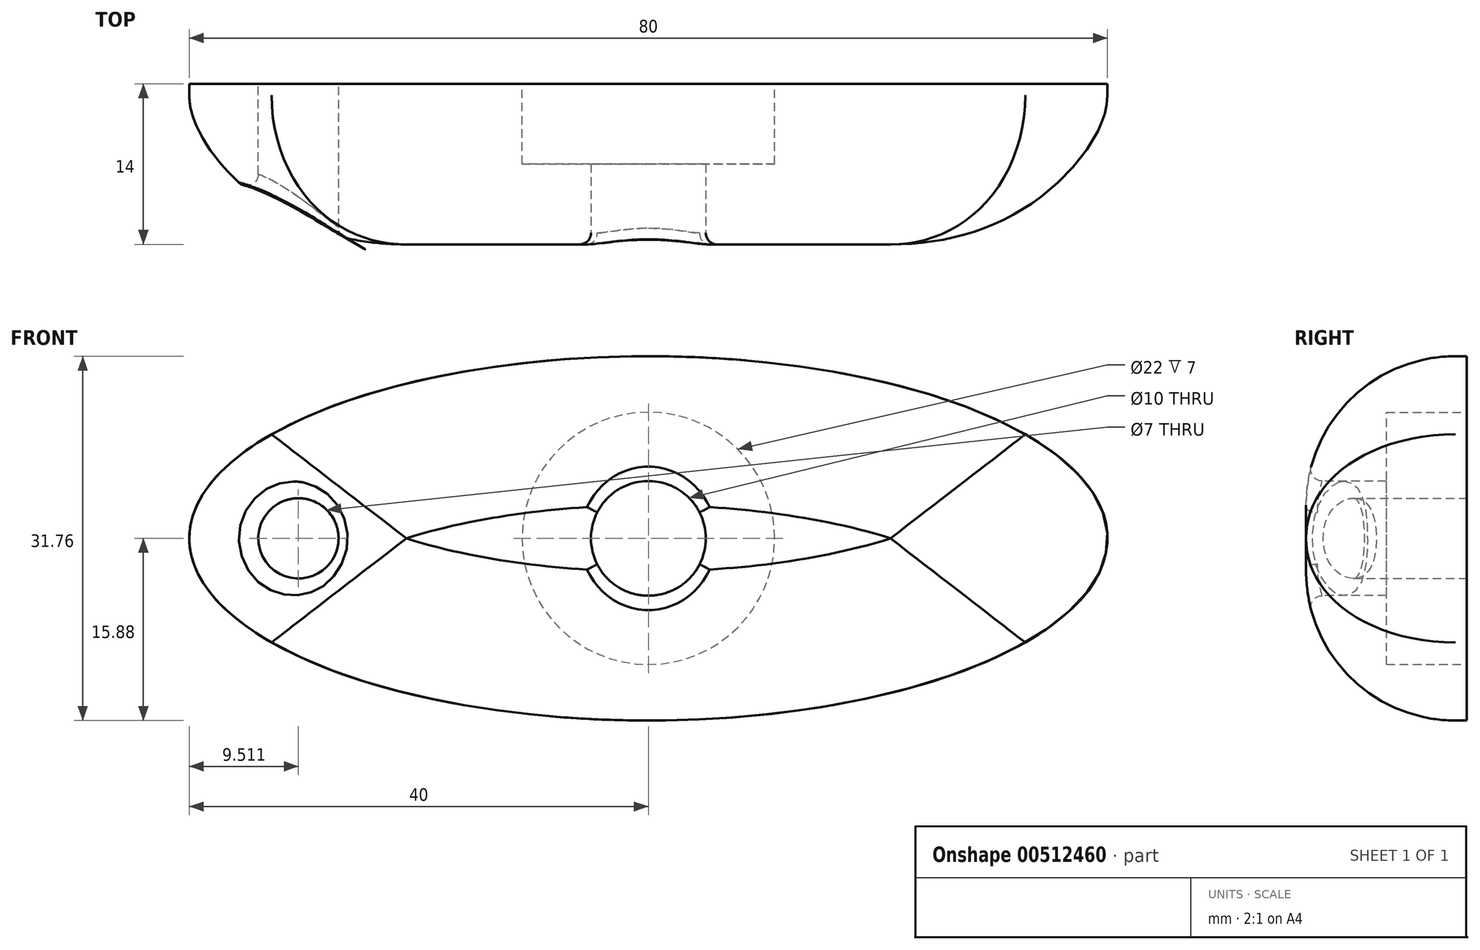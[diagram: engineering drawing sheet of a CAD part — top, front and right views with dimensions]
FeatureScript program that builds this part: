
annotation { "Feature Type Name" : "Feature", "Feature Type Description" : "" }
export const myFeature = defineFeature(function(context is Context, id is Id, definition is map)
    precondition{}
    {
        {
            var Q0;
            Q0=qCreatedBy(makeId("Front.planeOp"),FACE);
            var sketch = newSketch(context, id + "F0", { "sketchPlane" : qUnion([Q0])});
            skEllipse(sketch, "E0", {"center": v(0, 0) * mm, "majorRadius": 40 * mm, "minorRadius": 15.88 * mm, "majorAxis": v(-1, 0)});
            skCircle(sketch, "E1", {"center": v(0, 0) * mm, "radius": 11 * mm});
            skSolve(sketch);
        }
        {
            var Q0;
            Q0 = qSketchRegion(id + "F0", true);
            extrude(context, id + "F1", {"entities" : qUnion([Q0]), "depth" : 14 * mm});
        }
        {
            var Q0;
            Q0=makeQuery(id+"F1.opExtrude","CAP_FACE",FACE,{"disambiguationData":[OSD([sQuery(id+"F0.wireOp",EDGE,"E0"),sQuery(id+"F0.wireOp",EDGE,"E1")])],"isStart":false});
            var sketch = newSketch(context, id + "F2", { "sketchPlane" : qUnion([Q0])});
            skCircle(sketch, "E2", {"center": v(0, 0) * mm, "radius": 5 * mm});
            skSolve(sketch);
        }
        {
            var Q0;
            Q0=makeQuery(id+"F2.imprint","IMPRINT",FACE,{"disambiguationData":[TD([[makeQuery(id+"F2.imprint","IMPRINT",EDGE,{"derivedFrom":sQuery(id+"F2.wireOp",EDGE,"E2")}),-1.0]])]});
            extrude(context, id + "F3", {"entities" : qUnion([Q0]), "operationType" : NewBodyOperationType.ADD, "oppositeDirection" : true, "depth" : 7 * mm});
        }
        {
            var Q0;
            Q0=makeQuery(id+"F1.opExtrude","CAP_EDGE",EDGE,{"disambiguationData":[OSD([sQuery(id+"F0.wireOp",EDGE,"E0")])],"isStart":false});
            fillet(context, id + "F4", {"entities" : qUnion([Q0]), "radius" : 13 * mm, "tangentPropagation" : true, "allowEdgeOverflow" : false});
        }
        {
            var Q0;
            Q0=makeQuery(id+"F1.opExtrude","CAP_FACE",FACE,{"disambiguationData":[OSD([sQuery(id+"F0.wireOp",EDGE,"E0"),sQuery(id+"F0.wireOp",EDGE,"E1")])],"isStart":true});
            var sketch = newSketch(context, id + "F5", { "sketchPlane" : qUnion([Q0])});
            skCircle(sketch, "E3", {"center": v(30.49, 0) * mm, "radius": 3.5 * mm});
            skSolve(sketch);
        }
        {
            var Q0;
            Q0=makeQuery(id+"F5.imprint","IMPRINT",FACE,{"disambiguationData":[TD([[makeQuery(id+"F5.imprint","IMPRINT",EDGE,{"derivedFrom":sQuery(id+"F5.wireOp",EDGE,"E3")}),1.0]])]});
            extrude(context, id + "F6", {"entities" : qUnion([Q0]), "operationType" : NewBodyOperationType.REMOVE, "endBound" : BoundingType.THROUGH_ALL, "oppositeDirection" : true, "depth" : 25 * mm});
        }
        {
            var Q0;
            Q0=makeQuery(id+"F6.boolean.opBoolean","INTERSECT",EDGE,{"derivedFrom":[makeQuery(id+"F4.opFillet","BLEND_FACE",FACE,{"disambiguationData":[OSD([sQuery(id+"F0.wireOp",EDGE,"E0")]),OD(0.0)]}),makeQuery(id+"F6.opExtrude","SWEPT_FACE",FACE,{"disambiguationData":[OSD([sQuery(id+"F5.wireOp",EDGE,"E3")])]})]});
            fillet(context, id + "F7", {"entities" : qUnion([Q0]), "radius" : 1 * mm, "tangentPropagation" : true, "allowEdgeOverflow" : false});
        }
        {
            var Q0;
            Q0=makeQuery(id+"F4.opFillet","BLEND_EDGE",EDGE,{"disambiguationData":[OD(1.0)],"blendedFrom":[makeQuery(id+"F1.opExtrude","CAP_EDGE",EDGE,{"disambiguationData":[OSD([sQuery(id+"F0.wireOp",EDGE,"E0")])],"isStart":false}),makeQuery(id+"F3.opExtrude","SWEPT_FACE",FACE,{"disambiguationData":[OSD([sQuery(id+"F2.wireOp",EDGE,"E2")])]})],"blendedInto":[makeQuery(id+"F3.opExtrude","SWEPT_FACE",FACE,{"disambiguationData":[OSD([sQuery(id+"F2.wireOp",EDGE,"E2")])]})]});
            var Q1;
            Q1=makeQuery(id+"F3.opExtrude","CAP_EDGE",EDGE,{"disambiguationData":[OSD([sQuery(id+"F2.wireOp",EDGE,"E2")])],"isStart":true});
            var Q2;
            Q2=makeQuery(id+"F4.opFillet","BLEND_EDGE",EDGE,{"disambiguationData":[OD(0.0)],"blendedFrom":[makeQuery(id+"F1.opExtrude","CAP_EDGE",EDGE,{"disambiguationData":[OSD([sQuery(id+"F0.wireOp",EDGE,"E0")])],"isStart":false}),makeQuery(id+"F3.opExtrude","SWEPT_FACE",FACE,{"disambiguationData":[OSD([sQuery(id+"F2.wireOp",EDGE,"E2")])]})],"blendedInto":[makeQuery(id+"F3.opExtrude","SWEPT_FACE",FACE,{"disambiguationData":[OSD([sQuery(id+"F2.wireOp",EDGE,"E2")])]})]});
            fillet(context, id + "F8", {"entities" : qUnion([Q0, Q1, Q2]), "radius" : 1 * mm, "tangentPropagation" : true, "allowEdgeOverflow" : false});
        }
    });
